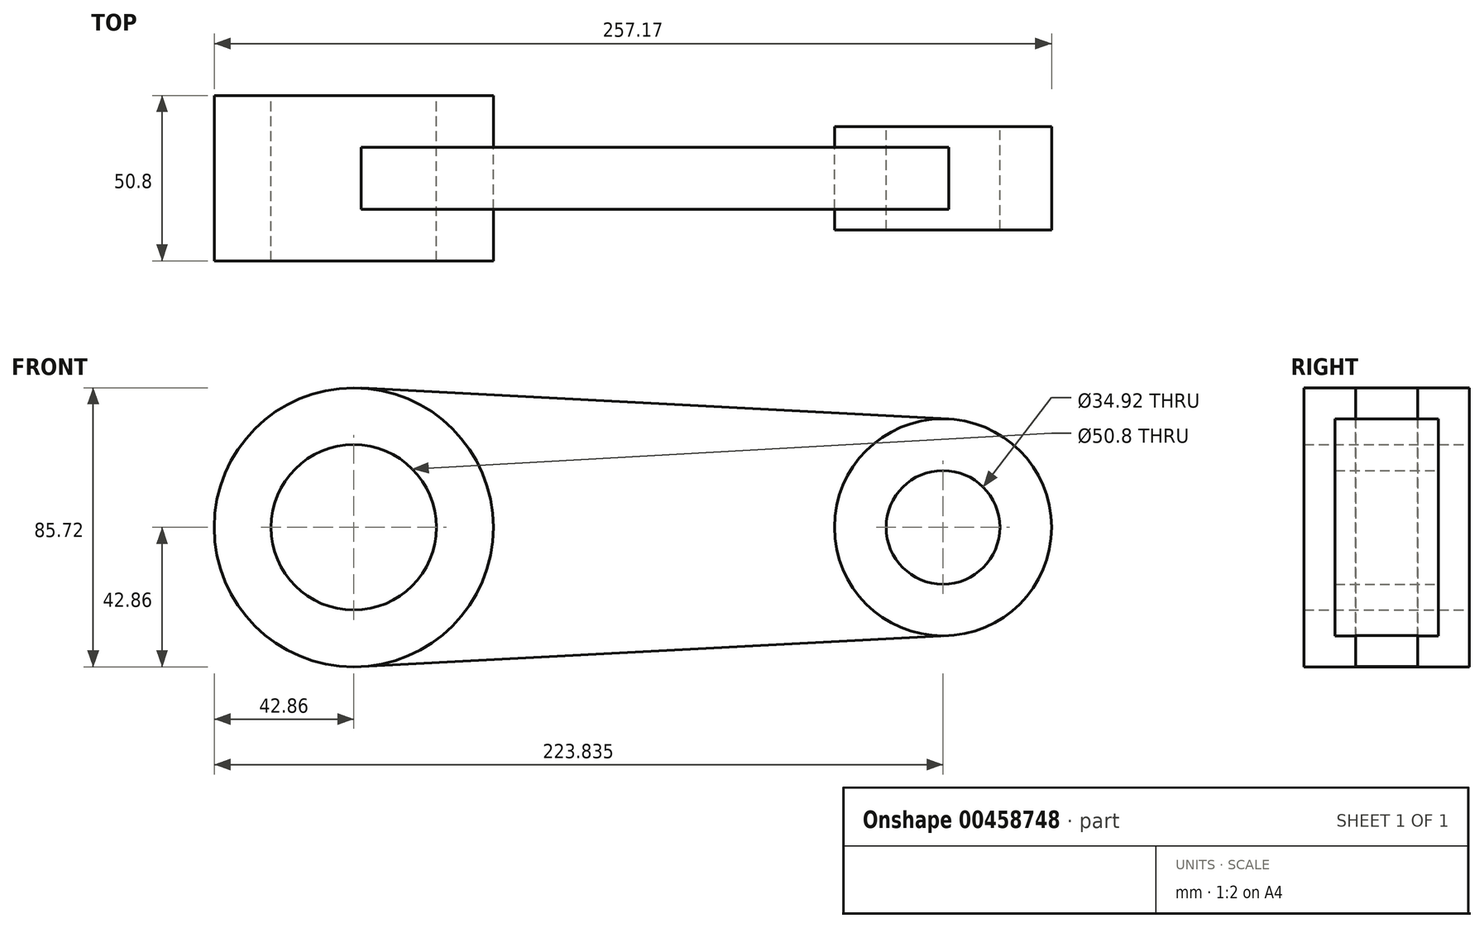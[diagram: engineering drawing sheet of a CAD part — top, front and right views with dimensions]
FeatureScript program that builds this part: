
annotation { "Feature Type Name" : "Feature", "Feature Type Description" : "" }
export const myFeature = defineFeature(function(context is Context, id is Id, definition is map)
    precondition{}
    {
        {
            var Q0;
            Q0=qCreatedBy(makeId("Front.planeOp"),FACE);
            var sketch = newSketch(context, id + "F0", { "sketchPlane" : qUnion([Q0])});
            skCircle(sketch, "E0", {"center": v(0, 0) * mm, "radius": 42.86 * mm});
            skCircle(sketch, "E1", {"center": v(0, 0) * mm, "radius": 25.4 * mm});
            skCircle(sketch, "E2", {"center": v(180.98, 0) * mm, "radius": 17.46 * mm});
            skCircle(sketch, "E3", {"center": v(180.98, 0) * mm, "radius": 33.34 * mm});
            skLineSegment(sketch, "E4", {"start": v(2.26, 42.8) * mm, "end": v(182.73, 33.3) * mm});
            skLineSegment(sketch, "E5", {"start": v(2.26, -42.8) * mm, "end": v(182.73, -33.3) * mm});
            skSolve(sketch);
        }
        {
            var Q0;
            Q0=makeQuery(id+"F0.imprint","IMPRINT",FACE,{"disambiguationData":[TD([[makeQuery(id+"F0.imprint","IMPRINT",EDGE,{"derivedFrom":sQuery(id+"F0.wireOp",EDGE,"E1")}),-1.0]])]});
            extrude(context, id + "F1", {"entities" : qUnion([Q0]), "depth" : 50.8 * mm, "symmetric" : true});
        }
        {
            var Q0;
            Q0=makeQuery(id+"F0.imprint","IMPRINT",FACE,{"disambiguationData":[TD([[makeQuery(id+"F0.imprint","IMPRINT",EDGE,{"derivedFrom":sQuery(id+"F0.wireOp",EDGE,"E2")}),-1.0]])]});
            extrude(context, id + "F2", {"entities" : qUnion([Q0]), "depth" : 31.75 * mm, "symmetric" : true});
        }
        {
            var Q0;
            {var subQ0=sQuery(id+"F0.wireOp",EDGE,"E4");Q0=makeQuery(id+"F0.imprint","IMPRINT",FACE,{"disambiguationData":[TD([[makeQuery(id+"F0.imprint","IMPRINT",EDGE,{"derivedFrom":subQ0}),-1.0]])]});}
            extrude(context, id + "F3", {"entities" : qUnion([Q0]), "depth" : 19.05 * mm, "symmetric" : true});
        }
    });
